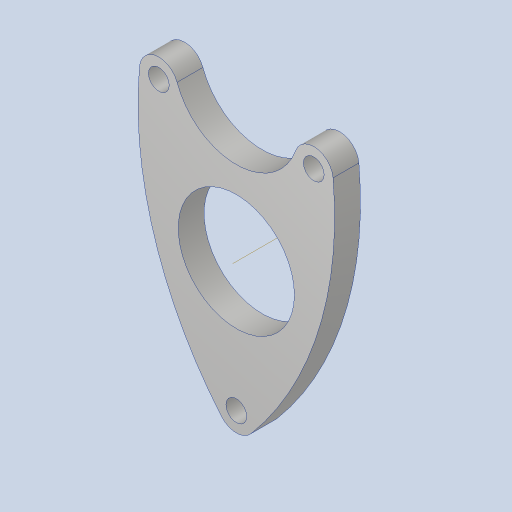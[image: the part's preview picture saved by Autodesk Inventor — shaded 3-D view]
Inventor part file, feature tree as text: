
AUTODESK INVENTOR PART (.ipt)
format: ipt  version: 2023.4 (Build 274418000, 418)  size: 137,728 bytes
history: native  units: in
note: dims shown in document units (in); Inventor stores cm internally (conversion verified against a paired STEP export)
features: sketch x1, extrude x1, hole x1, other x1
ambient origin geometry x8: Origin, YZ Plane, XZ Plane, XY Plane, X Axis, Y Axis, Z Axis, Center Point
bodies: Solid1 (feature_tree)
feature tree (4):
  sketch  "Sketch1"  dims[d0=1.125in d1=0.25in d2=0.375in d3=0.375in d4=0.375in d7=0.25in d8=0.375in d9=0.375in d13=0.75in d14=0.25in d15=0.0in d16=0.201in d17=0.75in d18=0.385in d19=0.25in d20=0.5635in d21=1.0in d22=0.8108in]
  extrude  "Extrusion1"  Depth=0.25in
  hole  "Hole1"  [1 undecoded]
  other  "Work Axis1"
note: 1 required parameter value undecoded (feature->parameter linkage not recoverable at this tier; creation-order binding heuristic only, values carry confidence <= 0.55)
